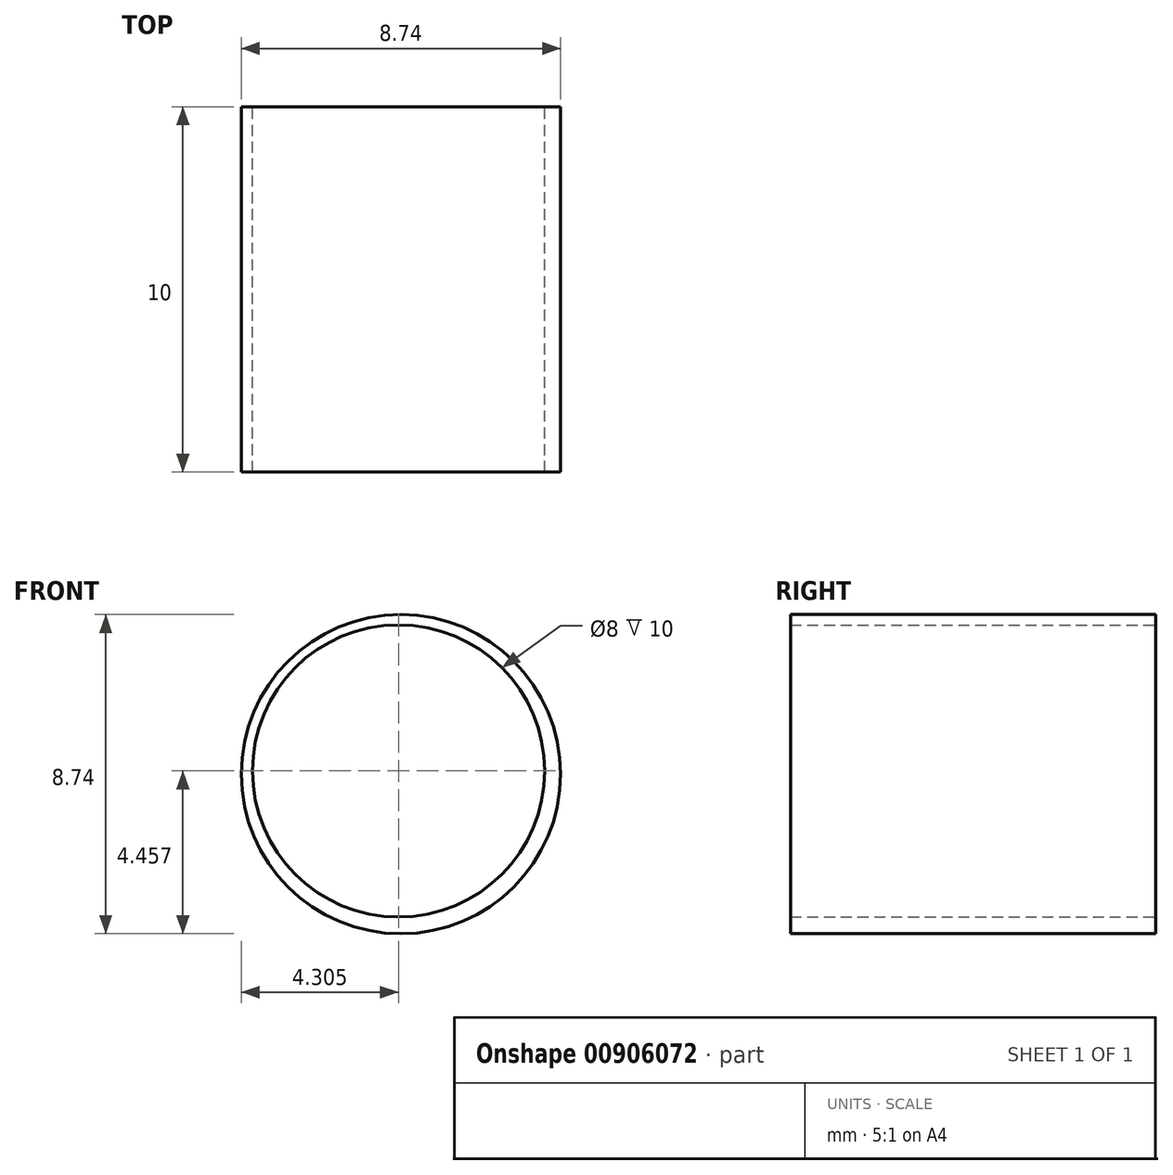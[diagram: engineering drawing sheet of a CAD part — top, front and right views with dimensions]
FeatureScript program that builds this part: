
annotation { "Feature Type Name" : "Feature", "Feature Type Description" : "" }
export const myFeature = defineFeature(function(context is Context, id is Id, definition is map)
    precondition{}
    {
        {
            var Q0;
            Q0=qCreatedBy(makeId("Front.planeOp"),FACE);
            var sketch = newSketch(context, id + "F0", { "sketchPlane" : qUnion([Q0])});
            skCircle(sketch, "E0", {"center": v(0, 0) * mm, "radius": 4.37 * mm});
            skCircle(sketch, "E1", {"center": v(-0.06, 0.09) * mm, "radius": 4 * mm});
            skSolve(sketch);
        }
        {
            var Q0;
            Q0=makeQuery(id+"F0.imprint","IMPRINT",FACE,{"disambiguationData":[TD([[makeQuery(id+"F0.imprint","IMPRINT",EDGE,{"derivedFrom":sQuery(id+"F0.wireOp",EDGE,"E0")}),1.0]])]});
            extrude(context, id + "F1", {"entities" : qUnion([Q0]), "depth" : 10 * mm, "offsetDistance" : 25 * mm});
        }
    });
